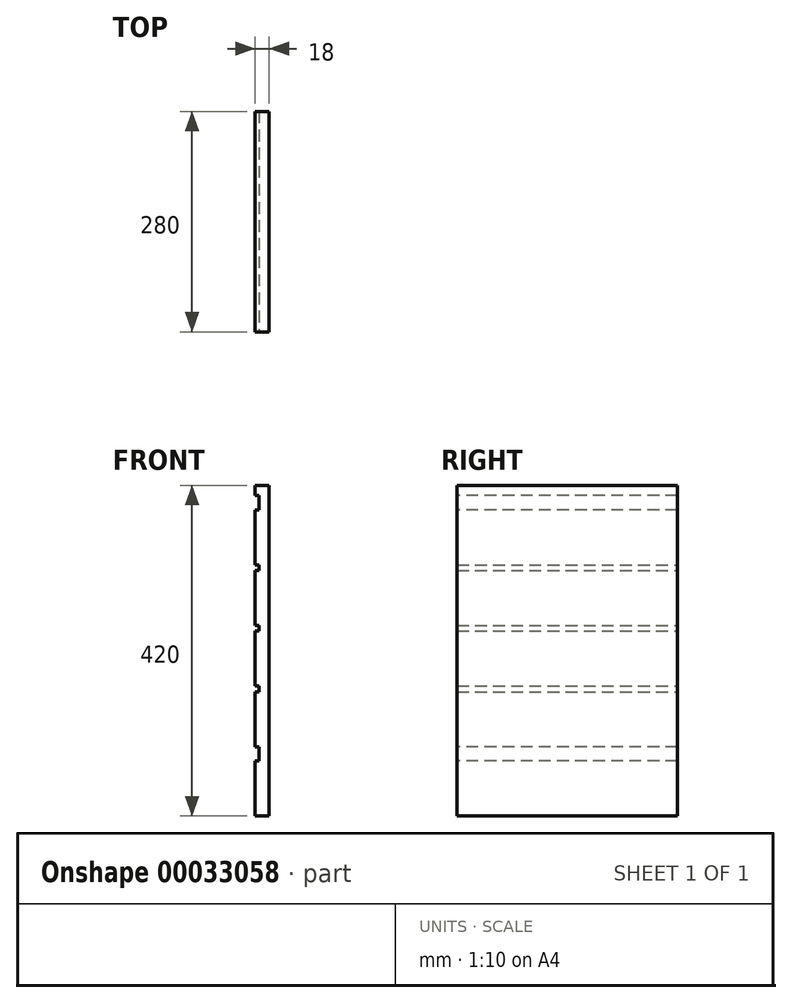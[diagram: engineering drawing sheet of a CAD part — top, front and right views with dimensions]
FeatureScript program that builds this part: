
annotation { "Feature Type Name" : "Feature", "Feature Type Description" : "" }
export const myFeature = defineFeature(function(context is Context, id is Id, definition is map)
    precondition{}
    {
        {
            var Q0;
            Q0=qCreatedBy(makeId("Right.planeOp"),FACE);
            var sketch = newSketch(context, id + "F0", { "sketchPlane" : qUnion([Q0])});
            skLineSegment(sketch, "E0.bottom", {"start": v(0, 0) * mm, "end": v(280, 0) * mm});
            skLineSegment(sketch, "E0.top", {"start": v(0, 420) * mm, "end": v(280, 420) * mm});
            skLineSegment(sketch, "E0.left", {"start": v(0, 0) * mm, "end": v(0, 420) * mm});
            skLineSegment(sketch, "E0.right", {"start": v(280, 0) * mm, "end": v(280, 420) * mm});
            skSolve(sketch);
        }
        {
            var Q0;
            Q0=makeQuery(id+"F0.imprint","IMPRINT",FACE,{"disambiguationData":[TD([[makeQuery(id+"F0.imprint","IMPRINT",EDGE,{"derivedFrom":sQuery(id+"F0.wireOp",EDGE,"E0.bottom")}),1.0]])]});
            extrude(context, id + "F1", {"entities" : qUnion([Q0]), "depth" : 18 * mm});
        }
        {
            var Q0;
            Q0=makeQuery(id+"F1.opExtrude","CAP_FACE",FACE,{"disambiguationData":[OSD([sQuery(id+"F0.wireOp",EDGE,"E0.bottom"),sQuery(id+"F0.wireOp",EDGE,"E0.top"),sQuery(id+"F0.wireOp",EDGE,"E0.left"),sQuery(id+"F0.wireOp",EDGE,"E0.right")])],"isStart":true});
            var sketch = newSketch(context, id + "F2", { "sketchPlane" : qUnion([Q0])});
            skLineSegment(sketch, "E1.bottom", {"start": v(-280, 70) * mm, "end": v(0, 70) * mm});
            skLineSegment(sketch, "E1.top", {"start": v(-280, 88) * mm, "end": v(0, 88) * mm});
            skLineSegment(sketch, "E1.left", {"start": v(-280, 70) * mm, "end": v(-280, 88) * mm});
            skLineSegment(sketch, "E1.right", {"start": v(0, 70) * mm, "end": v(0, 88) * mm});
            skLineSegment(sketch, "E2.bottom", {"start": v(0, 158) * mm, "end": v(-280, 158) * mm});
            skLineSegment(sketch, "E2.top", {"start": v(0, 165) * mm, "end": v(-280, 165) * mm});
            skLineSegment(sketch, "E2.left", {"start": v(0, 158) * mm, "end": v(0, 165) * mm});
            skLineSegment(sketch, "E2.right", {"start": v(-280, 158) * mm, "end": v(-280, 165) * mm});
            skLineSegment(sketch, "E3.bottom", {"start": v(0, 235) * mm, "end": v(-280, 235) * mm});
            skLineSegment(sketch, "E3.top", {"start": v(0, 242) * mm, "end": v(-280, 242) * mm});
            skLineSegment(sketch, "E3.left", {"start": v(0, 235) * mm, "end": v(0, 242) * mm});
            skLineSegment(sketch, "E3.right", {"start": v(-280, 235) * mm, "end": v(-280, 242) * mm});
            skLineSegment(sketch, "E4.bottom", {"start": v(0, 312) * mm, "end": v(-280, 312) * mm});
            skLineSegment(sketch, "E4.top", {"start": v(0, 319) * mm, "end": v(-280, 319) * mm});
            skLineSegment(sketch, "E4.left", {"start": v(0, 312) * mm, "end": v(0, 319) * mm});
            skLineSegment(sketch, "E4.right", {"start": v(-280, 312) * mm, "end": v(-280, 319) * mm});
            skLineSegment(sketch, "E5.bottom", {"start": v(-280, 407) * mm, "end": v(0, 407) * mm});
            skLineSegment(sketch, "E5.top", {"start": v(-280, 389) * mm, "end": v(0, 389) * mm});
            skLineSegment(sketch, "E5.left", {"start": v(-280, 407) * mm, "end": v(-280, 389) * mm});
            skLineSegment(sketch, "E5.right", {"start": v(0, 407) * mm, "end": v(0, 389) * mm});
            skSolve(sketch);
        }
        {
            var Q0;
            Q0 = qSketchRegion(id + "F2", true);
            extrude(context, id + "F3", {"entities" : qUnion([Q0]), "operationType" : NewBodyOperationType.REMOVE, "oppositeDirection" : true, "depth" : 5 * mm});
        }
    });
